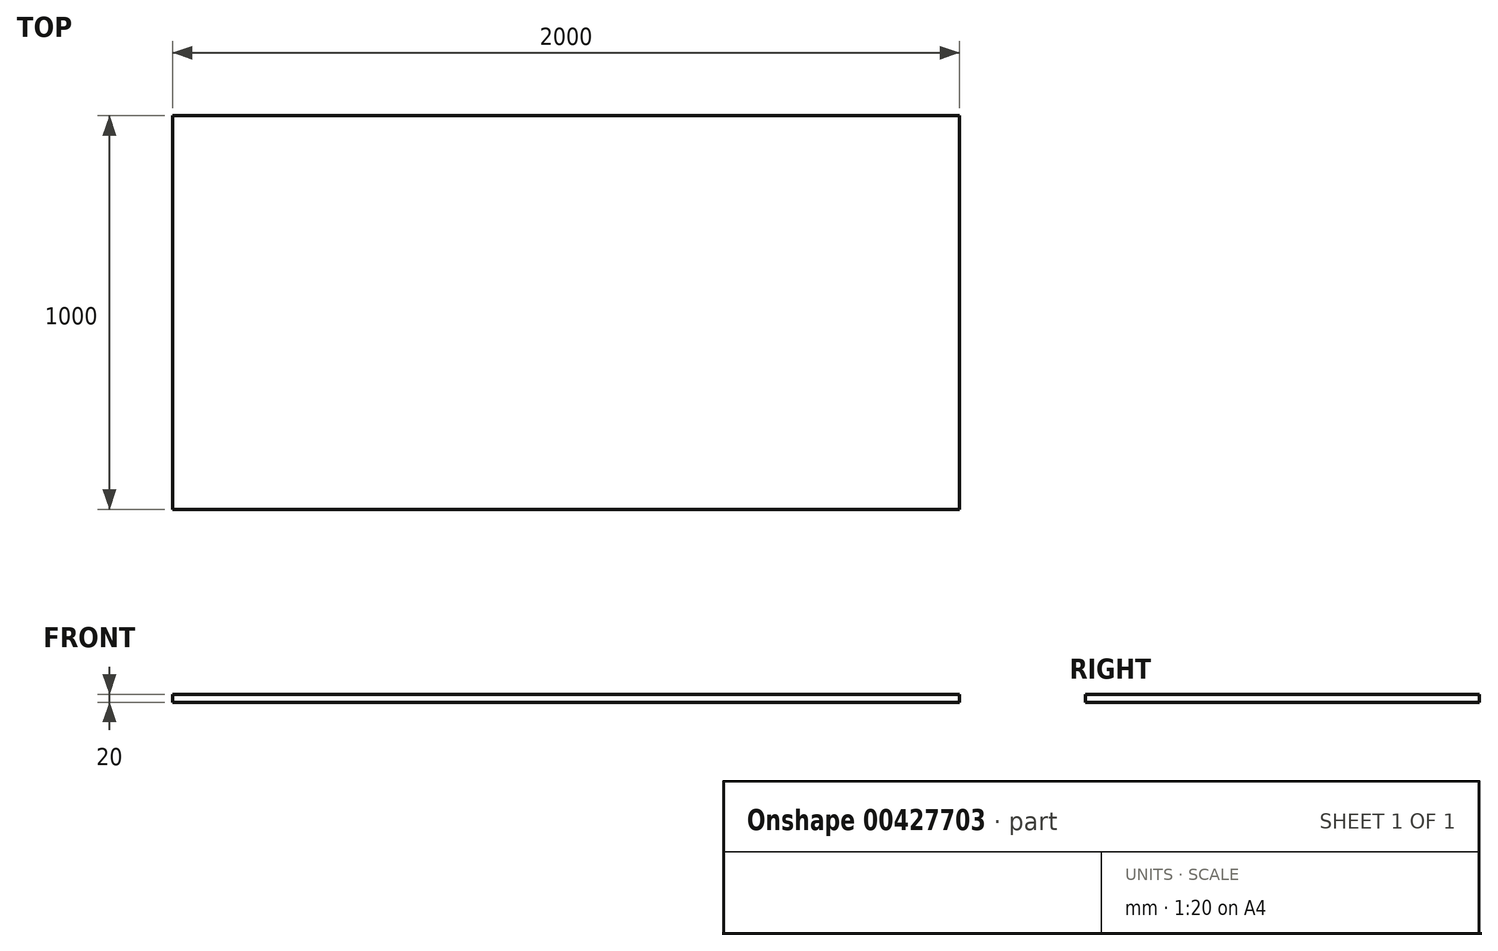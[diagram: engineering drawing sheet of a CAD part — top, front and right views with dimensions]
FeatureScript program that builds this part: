
annotation { "Feature Type Name" : "Feature", "Feature Type Description" : "" }
export const myFeature = defineFeature(function(context is Context, id is Id, definition is map)
    precondition{}
    {
        {
            var Q0;
            Q0=qCreatedBy(makeId("Front.planeOp"),FACE);
            var sketch = newSketch(context, id + "F0", { "sketchPlane" : qUnion([Q0])});
            skLineSegment(sketch, "E0.bottom", {"start": v(-1000, 10) * mm, "end": v(1000, 10) * mm});
            skLineSegment(sketch, "E0.top", {"start": v(-1000, -10) * mm, "end": v(1000, -10) * mm});
            skLineSegment(sketch, "E0.left", {"start": v(-1000, 10) * mm, "end": v(-1000, -10) * mm});
            skLineSegment(sketch, "E0.right", {"start": v(1000, 10) * mm, "end": v(1000, -10) * mm});
            skPoint(sketch, "E0.middle", {"position": v(0, 0) * mm});
            skSolve(sketch);
        }
        {
            var Q0;
            Q0=makeQuery(id+"F0.imprint","IMPRINT",FACE,{"disambiguationData":[TD([[makeQuery(id+"F0.imprint","IMPRINT",EDGE,{"derivedFrom":sQuery(id+"F0.wireOp",EDGE,"E0.bottom")}),-1.0]])]});
            extrude(context, id + "F1", {"entities" : qUnion([Q0]), "depth" : 1000 * mm});
        }
    });
